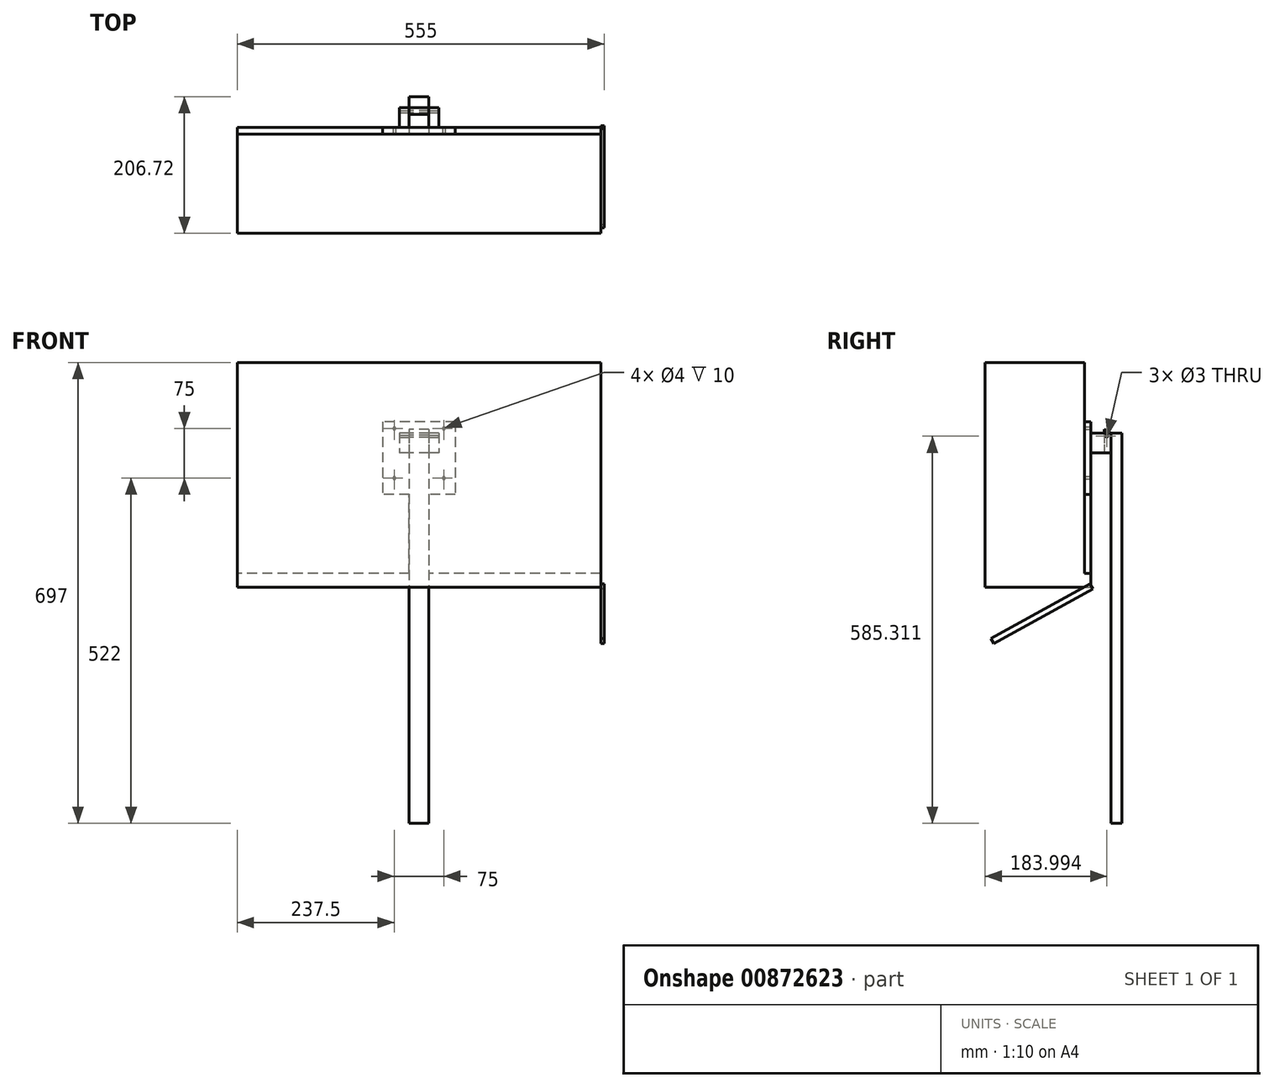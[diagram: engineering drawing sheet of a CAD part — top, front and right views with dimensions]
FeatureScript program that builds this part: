
annotation { "Feature Type Name" : "Feature", "Feature Type Description" : "" }
export const myFeature = defineFeature(function(context is Context, id is Id, definition is map)
    precondition{}
    {
        {
            var Q0;
            Q0=qCreatedBy(makeId("Front.planeOp"),FACE);
            var sketch = newSketch(context, id + "F0", { "sketchPlane" : qUnion([Q0])});
            skLineSegment(sketch, "E0.bottom", {"start": v(275, -170) * mm, "end": v(-275, -170) * mm});
            skLineSegment(sketch, "E0.top", {"start": v(275, 170) * mm, "end": v(-275, 170) * mm});
            skLineSegment(sketch, "E0.left", {"start": v(275, -170) * mm, "end": v(275, 170) * mm});
            skLineSegment(sketch, "E0.right", {"start": v(-275, -170) * mm, "end": v(-275, 170) * mm});
            skPoint(sketch, "E0.middle", {"position": v(0, 0) * mm});
            skSolve(sketch);
        }
        {
            var Q0;
            Q0 = qSketchRegion(id + "F0", true);
            extrude(context, id + "F1", {"entities" : qUnion([Q0]), "depth" : 150 * mm, "offsetDistance" : 25 * mm});
        }
        {
            var Q0;
            Q0=makeQuery(id+"F1.opExtrude","CAP_FACE",FACE,{"disambiguationData":[OSD([sQuery(id+"F0.wireOp",EDGE,"E0.bottom"),sQuery(id+"F0.wireOp",EDGE,"E0.top"),sQuery(id+"F0.wireOp",EDGE,"E0.left"),sQuery(id+"F0.wireOp",EDGE,"E0.right")])],"isStart":true});
            var sketch = newSketch(context, id + "F2", { "sketchPlane" : qUnion([Q0])});
            skLineSegment(sketch, "E1.bottom", {"start": v(-55, 80) * mm, "end": v(55, 80) * mm});
            skLineSegment(sketch, "E1.top", {"start": v(-55, -30) * mm, "end": v(55, -30) * mm});
            skLineSegment(sketch, "E1.left", {"start": v(-55, 80) * mm, "end": v(-55, -30) * mm});
            skLineSegment(sketch, "E1.right", {"start": v(55, 80) * mm, "end": v(55, -30) * mm});
            skLineSegment(sketch, "E2", {"start": v(-15, -30) * mm, "end": v(-15, -170) * mm});
            skLineSegment(sketch, "E3", {"start": v(-15, -170) * mm, "end": v(15, -170) * mm});
            skLineSegment(sketch, "E4", {"start": v(15, -170) * mm, "end": v(15, -30) * mm});
            skLineSegment(sketch, "E5", {"start": v(15, -149.3) * mm, "end": v(275, -149.3) * mm});
            skLineSegment(sketch, "E6", {"start": v(275, -149.3) * mm, "end": v(275, -170) * mm});
            skLineSegment(sketch, "E7", {"start": v(275, -170) * mm, "end": v(15, -170) * mm});
            skLineSegment(sketch, "E8", {"start": v(-275, -170) * mm, "end": v(-275, -149.3) * mm});
            skLineSegment(sketch, "E9", {"start": v(-275, -149.3) * mm, "end": v(-15, -149.3) * mm});
            skLineSegment(sketch, "E10", {"start": v(-15, -170) * mm, "end": v(-275, -170) * mm});
            skLineSegment(sketch, "E11.bottom", {"start": v(-30, 63) * mm, "end": v(-15, 63) * mm});
            skLineSegment(sketch, "E11.top", {"start": v(-30, 33) * mm, "end": v(-15, 33) * mm});
            skLineSegment(sketch, "E11.left", {"start": v(-30, 63) * mm, "end": v(-30, 33) * mm});
            skLineSegment(sketch, "E11.right", {"start": v(-15, 63) * mm, "end": v(-15, 33) * mm});
            skLineSegment(sketch, "E12.bottom", {"start": v(15, 63) * mm, "end": v(30, 63) * mm});
            skLineSegment(sketch, "E12.top", {"start": v(15, 33) * mm, "end": v(30, 33) * mm});
            skLineSegment(sketch, "E12.left", {"start": v(15, 63) * mm, "end": v(15, 33) * mm});
            skLineSegment(sketch, "E12.right", {"start": v(30, 63) * mm, "end": v(30, 33) * mm});
            skLineSegment(sketch, "E13.bottom", {"start": v(-37.5, 70) * mm, "end": v(37.5, 70) * mm});
            skLineSegment(sketch, "E13.top", {"start": v(-37.5, -5) * mm, "end": v(37.5, -5) * mm});
            skLineSegment(sketch, "E13.left", {"start": v(-37.5, 70) * mm, "end": v(-37.5, -5) * mm});
            skLineSegment(sketch, "E13.right", {"start": v(37.5, 70) * mm, "end": v(37.5, -5) * mm});
            skCircle(sketch, "E14", {"center": v(-37.5, 70) * mm, "radius": 2 * mm});
            skCircle(sketch, "E15", {"center": v(37.5, 70) * mm, "radius": 2 * mm});
            skCircle(sketch, "E16", {"center": v(37.5, -5) * mm, "radius": 2 * mm});
            skCircle(sketch, "E17", {"center": v(-37.5, -5) * mm, "radius": 2 * mm});
            skSolve(sketch);
        }
        {
            var Q0;
            Q0 = qSketchRegion(id + "F2", true);
            var Q1;
            Q1=makeQuery(id+"F2.imprint","IMPRINT",FACE,{"disambiguationData":[TD([[makeQuery(id+"F2.imprint","IMPRINT",EDGE,{"derivedFrom":sQuery(id+"F2.wireOp",EDGE,"E11.bottom")}),1.0]])]});
            extrude(context, id + "F3", {"entities" : qUnion([Q0, Q1]), "depth" : 10 * mm, "offsetDistance" : 25 * mm});
        }
        {
            var Q0;
            Q0=makeQuery(id+"F2.imprint","IMPRINT",FACE,{"disambiguationData":[TD([[makeQuery(id+"F2.imprint","IMPRINT",EDGE,{"derivedFrom":sQuery(id+"F2.wireOp",EDGE,"E11.bottom")}),-1.0]])]});
            var Q1;
            Q1=makeQuery(id+"F2.imprint","IMPRINT",FACE,{"disambiguationData":[TD([[makeQuery(id+"F2.imprint","IMPRINT",EDGE,{"derivedFrom":sQuery(id+"F2.wireOp",EDGE,"E12.bottom")}),-1.0]])]});
            extrude(context, id + "F4", {"entities" : qUnion([Q0, Q1]), "operationType" : NewBodyOperationType.ADD, "depth" : 40 * mm, "offsetDistance" : 25 * mm});
        }
        {
            var Q0;
            Q0=makeQuery(id+"F4.opExtrude","SWEPT_FACE",FACE,{"disambiguationData":[OSD([sQuery(id+"F2.wireOp",EDGE,"E11.left")])]});
            var sketch = newSketch(context, id + "F5", { "sketchPlane" : qUnion([Q0])});
            skCircle(sketch, "E18", {"center": v(34, 58.31) * mm, "radius": 1.5 * mm});
            skSolve(sketch);
        }
        {
            var Q0;
            Q0 = qSketchRegion(id + "F5", true);
            extrude(context, id + "F6", {"entities" : qUnion([Q0]), "operationType" : NewBodyOperationType.REMOVE, "endBound" : BoundingType.THROUGH_ALL, "oppositeDirection" : true, "depth" : 25 * mm, "offsetDistance" : 25 * mm});
        }
        {
            var Q0;
            Q0=makeQuery(id+"F4.opExtrude","SWEPT_FACE",FACE,{"disambiguationData":[OSD([sQuery(id+"F2.wireOp",EDGE,"E12.left")])]});
            var sketch = newSketch(context, id + "F7", { "sketchPlane" : qUnion([Q0])});
            skLineSegment(sketch, "E19.bottom", {"start": v(30.04, 63) * mm, "end": v(40, 63) * mm});
            skLineSegment(sketch, "E19.top", {"start": v(30.04, 33) * mm, "end": v(40, 33) * mm});
            skLineSegment(sketch, "E19.left", {"start": v(30.04, 63) * mm, "end": v(30.04, 33) * mm});
            skLineSegment(sketch, "E19.right", {"start": v(40, 63) * mm, "end": v(40, 33) * mm});
            skLineSegment(sketch, "E20.bottom", {"start": v(40, 63) * mm, "end": v(56.72, 63) * mm});
            skLineSegment(sketch, "E20.top", {"start": v(40, -527) * mm, "end": v(56.72, -527) * mm});
            skLineSegment(sketch, "E20.left", {"start": v(40, 63) * mm, "end": v(40, -527) * mm});
            skLineSegment(sketch, "E20.right", {"start": v(56.72, 63) * mm, "end": v(56.72, -527) * mm});
            skLineSegment(sketch, "E21", {"start": v(30.04, 63) * mm, "end": v(30.04, 68.63) * mm});
            skLineSegment(sketch, "E22", {"start": v(30.04, 68.63) * mm, "end": v(40, 63) * mm});
            skSolve(sketch);
        }
        {
            var Q0;
            {var subQ1=sQuery(id+"F7.wireOp",EDGE,"E19.bottom");Q0=makeQuery(id+"F7.imprint","IMPRINT",FACE,{"disambiguationData":[TD([[makeQuery(id+"F7.imprint","IMPRINT",EDGE,{"derivedFrom":subQ1}),1.0]])]});}
            var Q1;
            Q1=makeQuery(id+"F7.imprint","IMPRINT",FACE,{"disambiguationData":[TD([[makeQuery(id+"F7.imprint","IMPRINT",EDGE,{"derivedFrom":sQuery(id+"F7.wireOp",EDGE,"E19.bottom")}),-1.0]])]});
            extrude(context, id + "F8", {"entities" : qUnion([Q0, Q1]), "depth" : 30 * mm, "offsetDistance" : 25 * mm});
        }
        {
            var Q0;
            {var subQ1=sQuery(id+"F7.wireOp",EDGE,"E20.bottom");Q0=makeQuery(id+"F7.imprint","IMPRINT",FACE,{"disambiguationData":[TD([[makeQuery(id+"F7.imprint","IMPRINT",EDGE,{"derivedFrom":subQ1}),-1.0]])]});}
            extrude(context, id + "F9", {"entities" : qUnion([Q0]), "depth" : 30 * mm, "offsetDistance" : 25 * mm});
        }
        {
            var Q0;
            Q0=makeQuery(id+"F3.opExtrude","SWEPT_FACE",FACE,{"disambiguationData":[OSD([sQuery(id+"F2.wireOp",EDGE,"E8")])]});
            var sketch = newSketch(context, id + "F10", { "sketchPlane" : qUnion([Q0])});
            skLineSegment(sketch, "E23", {"start": v(8.58, -164.87) * mm, "end": v(-141.35, -247.42) * mm});
            skLineSegment(sketch, "E24", {"start": v(-141.35, -247.42) * mm, "end": v(-137.01, -255.3) * mm});
            skLineSegment(sketch, "E25", {"start": v(-137.01, -255.3) * mm, "end": v(12.92, -172.75) * mm});
            skLineSegment(sketch, "E26", {"start": v(8.58, -164.87) * mm, "end": v(12.92, -172.75) * mm});
            skSolve(sketch);
        }
        {
            var Q0;
            Q0 = qSketchRegion(id + "F10", true);
            extrude(context, id + "F11", {"entities" : qUnion([Q0]), "depth" : 5 * mm, "offsetDistance" : 25 * mm});
        }
    });
